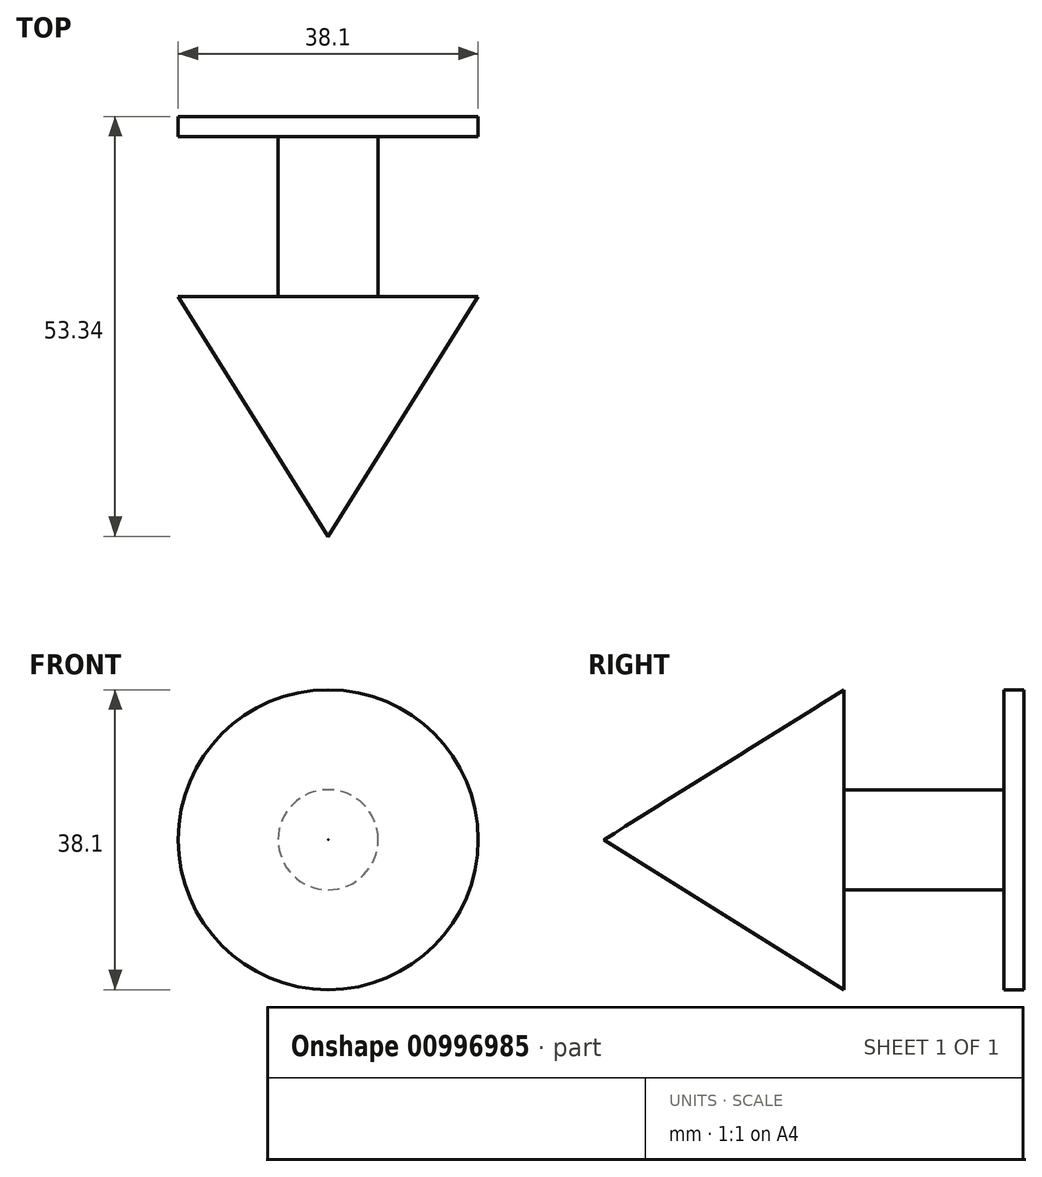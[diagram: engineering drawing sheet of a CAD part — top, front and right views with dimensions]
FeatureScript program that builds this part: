
annotation { "Feature Type Name" : "Feature", "Feature Type Description" : "" }
export const myFeature = defineFeature(function(context is Context, id is Id, definition is map)
    precondition{}
    {
        {
            var Q0;
            Q0=qCreatedBy(makeId("Front.planeOp"),FACE);
            var sketch = newSketch(context, id + "F0", { "sketchPlane" : qUnion([Q0])});
            skCircle(sketch, "E0", {"center": v(0, 0) * mm, "radius": 19.05 * mm});
            skSolve(sketch);
        }
        {
            var Q0;
            Q0 = qSketchRegion(id + "F0", true);
            extrude(context, id + "F1", {"entities" : qUnion([Q0]), "depth" : 2.54 * mm, "offsetDistance" : 25.4 * mm});
        }
        {
            var Q0;
            Q0=makeQuery(id+"F1.opExtrude","CAP_FACE",FACE,{"disambiguationData":[OSD([sQuery(id+"F0.wireOp",EDGE,"E0")])],"isStart":false});
            var sketch = newSketch(context, id + "F2", { "sketchPlane" : qUnion([Q0])});
            skCircle(sketch, "E1", {"center": v(0, 0) * mm, "radius": 6.35 * mm});
            skSolve(sketch);
        }
        {
            var Q0;
            Q0=makeQuery(id+"F2.imprint","IMPRINT",FACE,{"disambiguationData":[TD([[makeQuery(id+"F2.imprint","IMPRINT",EDGE,{"derivedFrom":sQuery(id+"F2.wireOp",EDGE,"E1")}),1.0]])]});
            extrude(context, id + "F3", {"entities" : qUnion([Q0]), "operationType" : NewBodyOperationType.ADD, "depth" : 20.32 * mm, "offsetDistance" : 25.4 * mm});
        }
        {
            var Q0;
            Q0=makeQuery(id+"F1.opExtrude","CAP_FACE",FACE,{"disambiguationData":[OSD([sQuery(id+"F0.wireOp",EDGE,"E0")])],"isStart":true});
            cPlane(context, id + "F4", {"entities" : qUnion([Q0]), "cplaneType" : CPlaneType.OFFSET, "offset" : 22.86 * mm, "oppositeDirection" : true, "width" : 152.4 * mm, "height" : 152.4 * mm});
        }
        {
            var Q0;
            Q0=qCreatedBy(id+"F4.planeOp",FACE);
            var sketch = newSketch(context, id + "F5", { "sketchPlane" : qUnion([Q0])});
            skLineSegment(sketch, "E2.bottom", {"start": v(23.1, 22.86) * mm, "end": v(-22.86, 22.86) * mm});
            skLineSegment(sketch, "E2.top", {"start": v(23.1, -22.86) * mm, "end": v(-22.86, -22.86) * mm});
            skLineSegment(sketch, "E2.left", {"start": v(23.1, 22.86) * mm, "end": v(23.1, -22.86) * mm});
            skLineSegment(sketch, "E2.right", {"start": v(-22.86, 22.86) * mm, "end": v(-22.86, -22.86) * mm});
            skCircle(sketch, "E3", {"center": v(0, 0) * mm, "radius": 19.05 * mm});
            skSolve(sketch);
        }
        {
            var Q0;
            Q0=makeQuery(id+"F5.imprint","IMPRINT",FACE,{"disambiguationData":[TD([[makeQuery(id+"F5.imprint","IMPRINT",EDGE,{"derivedFrom":sQuery(id+"F5.wireOp",EDGE,"E3")}),1.0]])]});
            extrude(context, id + "F6", {"entities" : qUnion([Q0]), "operationType" : NewBodyOperationType.ADD, "oppositeDirection" : true, "depth" : 30.48 * mm, "offsetDistance" : 25.4 * mm, "hasDraft" : true, "draftAngle" : 32 * degree, "draftPullDirection" : true});
        }
    });
